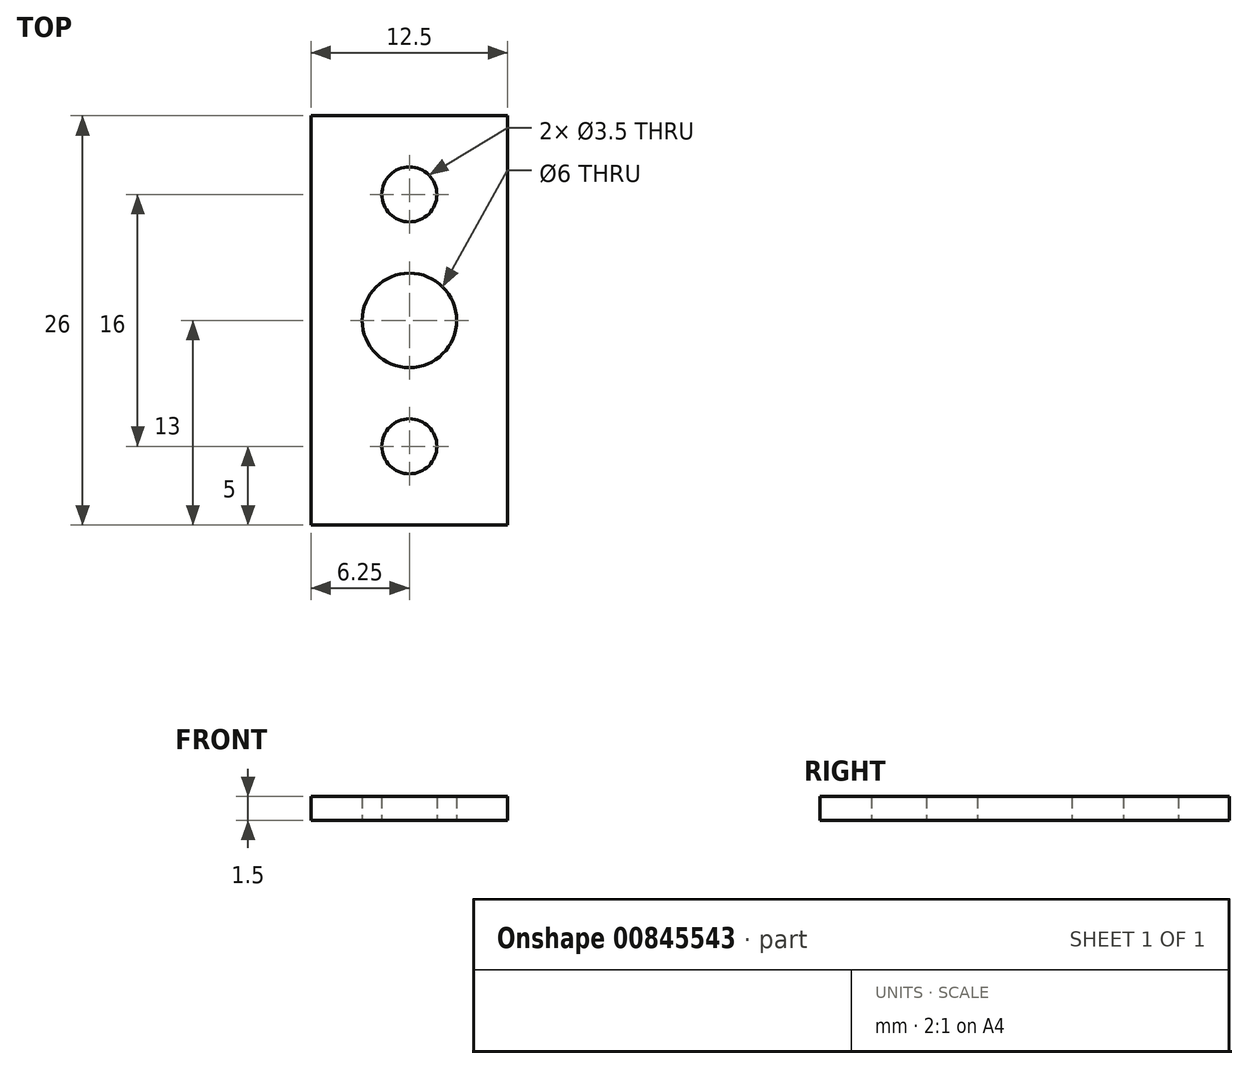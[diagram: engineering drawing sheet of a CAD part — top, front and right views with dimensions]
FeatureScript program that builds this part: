
annotation { "Feature Type Name" : "Feature", "Feature Type Description" : "" }
export const myFeature = defineFeature(function(context is Context, id is Id, definition is map)
    precondition{}
    {
        {
            var Q0;
            Q0=qCreatedBy(makeId("Top.planeOp"),FACE);
            var sketch = newSketch(context, id + "F0", { "sketchPlane" : qUnion([Q0])});
            skLineSegment(sketch, "E0.bottom", {"start": v(6.25, 13) * mm, "end": v(-6.25, 13) * mm});
            skLineSegment(sketch, "E0.top", {"start": v(6.25, -13) * mm, "end": v(-6.25, -13) * mm});
            skLineSegment(sketch, "E0.left", {"start": v(6.25, 13) * mm, "end": v(6.25, -13) * mm});
            skLineSegment(sketch, "E0.right", {"start": v(-6.25, 13) * mm, "end": v(-6.25, -13) * mm});
            skPoint(sketch, "E0.middle", {"position": v(0, 0) * mm});
            skCircle(sketch, "E1", {"center": v(0, 8) * mm, "radius": 1.75 * mm});
            skCircle(sketch, "E2", {"center": v(0, -8) * mm, "radius": 1.75 * mm});
            skCircle(sketch, "E3", {"center": v(0, 0) * mm, "radius": 3 * mm});
            skSolve(sketch);
        }
        {
            var Q0;
            Q0=makeQuery(id+"F0.imprint","IMPRINT",FACE,{"disambiguationData":[TD([[makeQuery(id+"F0.imprint","IMPRINT",EDGE,{"derivedFrom":sQuery(id+"F0.wireOp",EDGE,"E0.bottom")}),1.0]])]});
            extrude(context, id + "F1", {"entities" : qUnion([Q0]), "depth" : 1.5 * mm, "offsetDistance" : 25 * mm});
        }
    });
